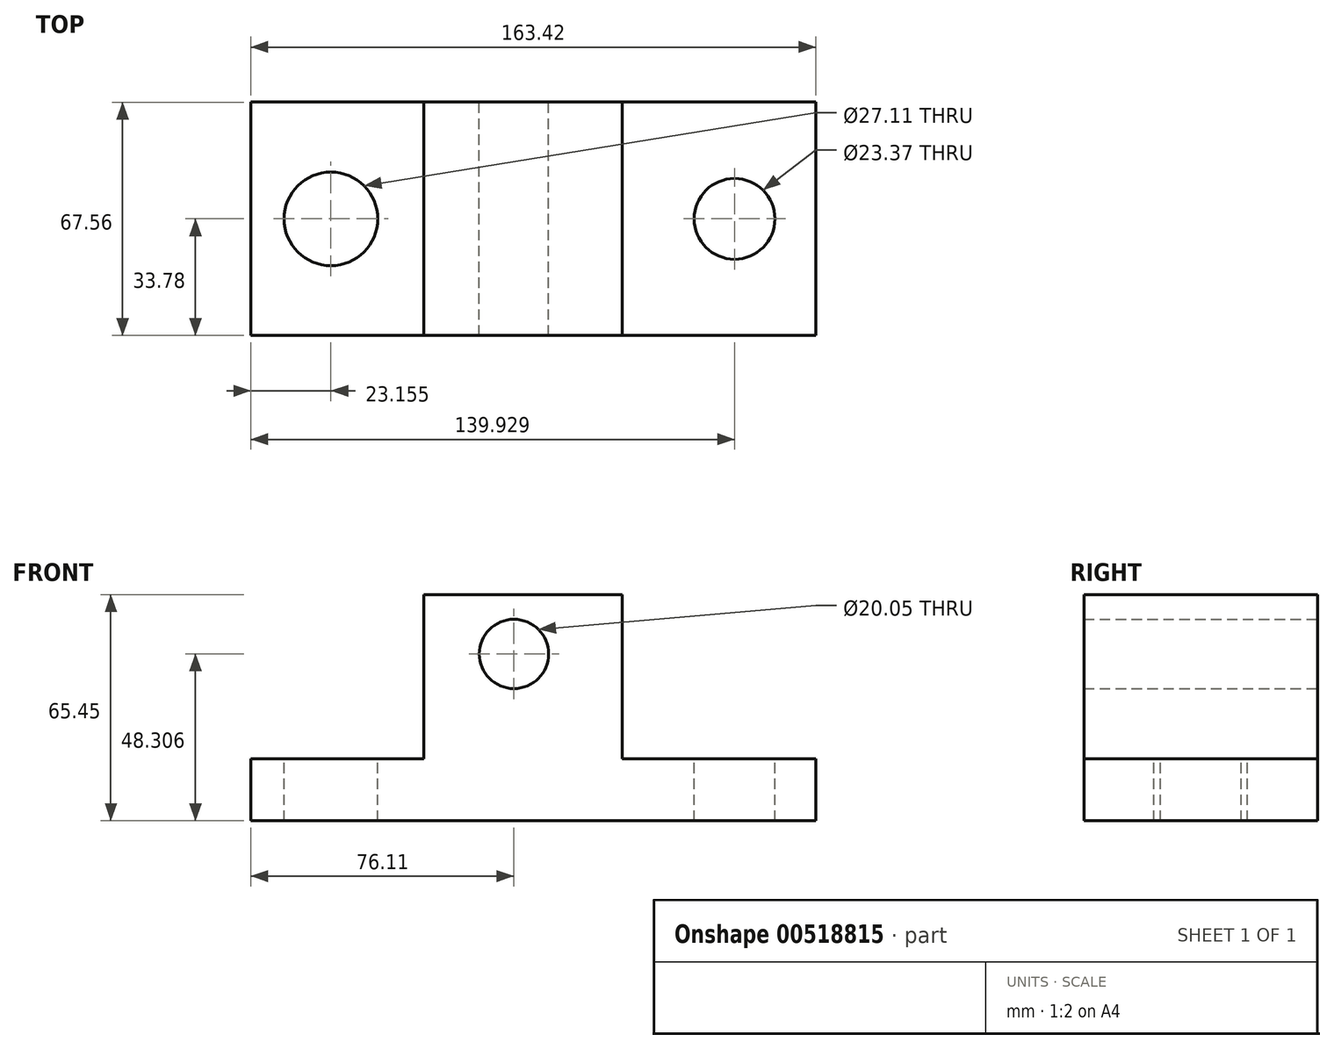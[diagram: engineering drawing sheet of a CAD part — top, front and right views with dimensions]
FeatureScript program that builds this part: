
annotation { "Feature Type Name" : "Feature", "Feature Type Description" : "" }
export const myFeature = defineFeature(function(context is Context, id is Id, definition is map)
    precondition{}
    {
        {
            var Q0;
            Q0=qCreatedBy(makeId("Front.planeOp"),FACE);
            var sketch = newSketch(context, id + "F0", { "sketchPlane" : qUnion([Q0])});
            skLineSegment(sketch, "E0", {"start": v(-76.1, 0) * mm, "end": v(-76.1, 18.01) * mm});
            skLineSegment(sketch, "E1", {"start": v(-76.1, 18.01) * mm, "end": v(-26.03, 18.01) * mm});
            skLineSegment(sketch, "E2", {"start": v(-26.03, 18.01) * mm, "end": v(-26.03, 65.45) * mm});
            skLineSegment(sketch, "E3", {"start": v(-26.03, 65.45) * mm, "end": v(31.3, 65.45) * mm});
            skLineSegment(sketch, "E4", {"start": v(31.3, 65.45) * mm, "end": v(31.3, 18.01) * mm});
            skLineSegment(sketch, "E5", {"start": v(31.3, 18.01) * mm, "end": v(87.3, 18.01) * mm});
            skLineSegment(sketch, "E6", {"start": v(87.3, 18.01) * mm, "end": v(87.3, 0) * mm});
            skLineSegment(sketch, "E7", {"start": v(87.3, 0) * mm, "end": v(-76.1, 0) * mm});
            skCircle(sketch, "E8", {"center": v(0, 48.3) * mm, "radius": 10.03 * mm});
            skSolve(sketch);
        }
        {
            var Q0;
            Q0 = qSketchRegion(id + "F0", true);
            extrude(context, id + "F1", {"entities" : qUnion([Q0]), "endBound" : BoundingType.SYMMETRIC, "depth" : 67.56 * mm, "offsetDistance" : 25.4 * mm});
        }
        {
            var Q0;
            Q0 = qSketchRegion(id + "F0", true);
            extrude(context, id + "F2", {"entities" : qUnion([Q0]), "operationType" : NewBodyOperationType.ADD, "depth" : 25.4 * mm, "offsetDistance" : 25.4 * mm});
        }
        {
            var Q0;
            Q0=makeQuery(id+"F1.opExtrude","SWEPT_FACE",FACE,{"disambiguationData":[OSD([sQuery(id+"F0.wireOp",EDGE,"E1")])]});
            var sketch = newSketch(context, id + "F3", { "sketchPlane" : qUnion([Q0])});
            skCircle(sketch, "E9", {"center": v(-52.96, 0) * mm, "radius": 13.56 * mm});
            skCircle(sketch, "E10", {"center": v(63.82, 0) * mm, "radius": 11.69 * mm});
            skSolve(sketch);
        }
        {
            var Q0;
            Q0 = qSketchRegion(id + "F3", true);
            extrude(context, id + "F4", {"entities" : qUnion([Q0]), "operationType" : NewBodyOperationType.REMOVE, "oppositeDirection" : true, "depth" : 25.4 * mm, "offsetDistance" : 25.4 * mm});
        }
        {
            var Q0;
            Q0 = qSketchRegion(id + "F3", true);
            extrude(context, id + "F5", {"entities" : qUnion([Q0]), "operationType" : NewBodyOperationType.REMOVE, "oppositeDirection" : true, "depth" : 25.4 * mm, "offsetDistance" : 25.4 * mm});
        }
    });
